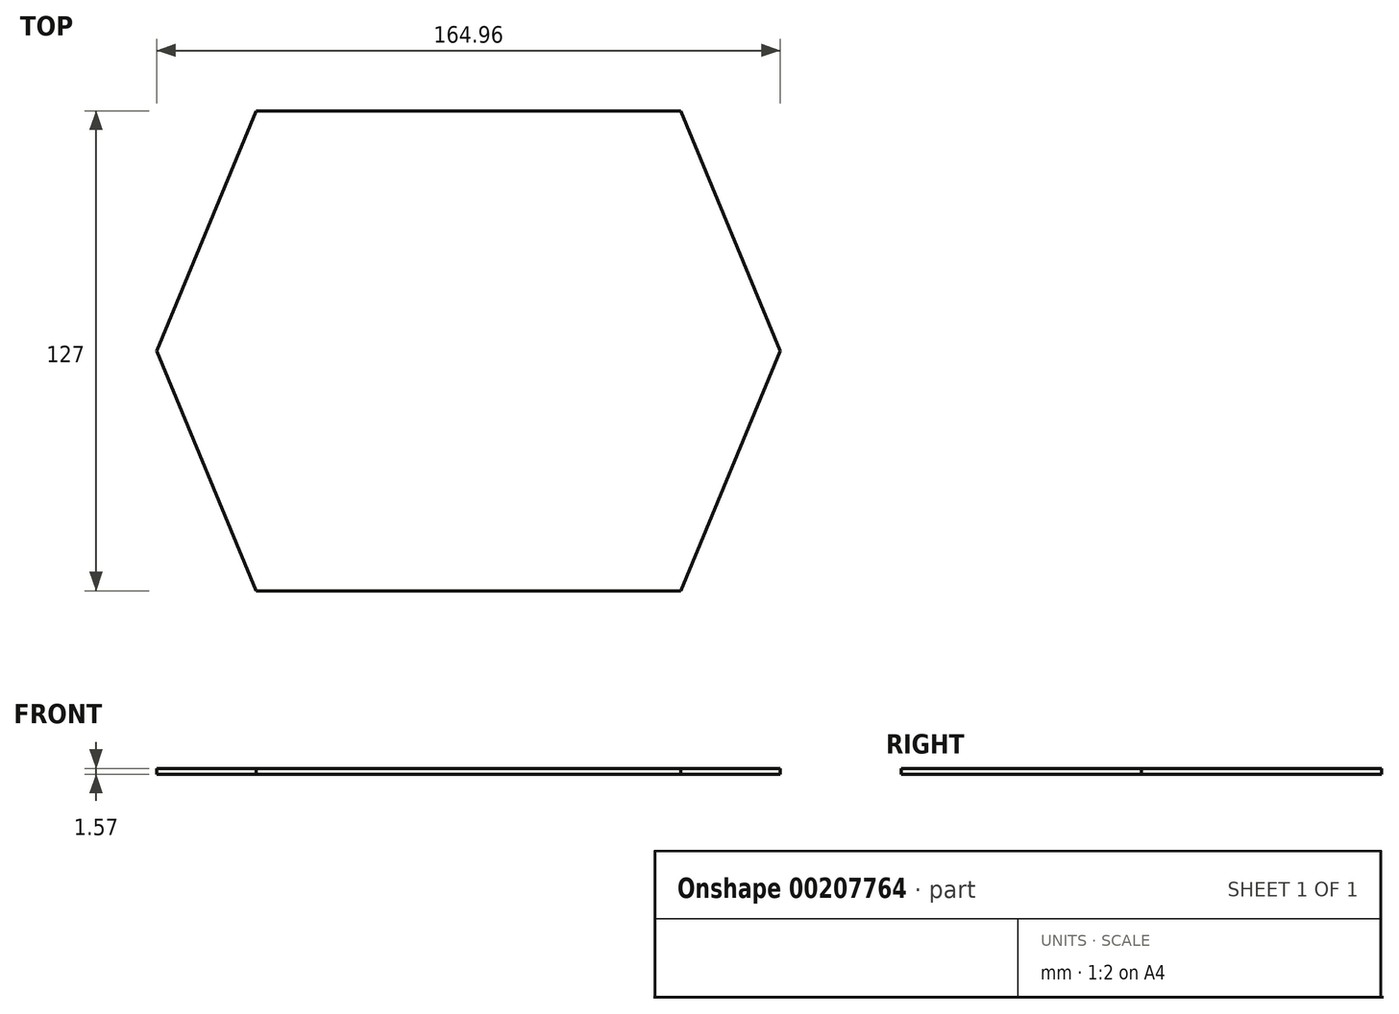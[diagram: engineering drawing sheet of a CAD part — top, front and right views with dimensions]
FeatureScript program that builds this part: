
annotation { "Feature Type Name" : "Feature", "Feature Type Description" : "" }
export const myFeature = defineFeature(function(context is Context, id is Id, definition is map)
    precondition{}
    {
        {
            var Q0;
            Q0=qCreatedBy(makeId("Top.planeOp"),FACE);
            var sketch = newSketch(context, id + "F0", { "sketchPlane" : qUnion([Q0])});
            skLineSegment(sketch, "E0", {"start": v(-56.18, 63.5) * mm, "end": v(56.18, 63.5) * mm});
            skLineSegment(sketch, "E1", {"start": v(-56.18, -63.5) * mm, "end": v(56.18, -63.5) * mm});
            skLineSegment(sketch, "E2", {"start": v(56.18, -63.5) * mm, "end": v(82.48, 0) * mm});
            skLineSegment(sketch, "E3", {"start": v(82.48, 0) * mm, "end": v(56.18, 63.5) * mm});
            skLineSegment(sketch, "E4", {"start": v(-56.18, -63.5) * mm, "end": v(-82.48, 0) * mm});
            skLineSegment(sketch, "E5", {"start": v(-82.48, 0) * mm, "end": v(-56.18, 63.5) * mm});
            skLineSegment(sketch, "E6", {"start": v(-82.48, 0) * mm, "end": v(82.48, 0) * mm, "construction": true});
            skSolve(sketch);
        }
        {
            var Q0;
            Q0 = qSketchRegion(id + "F0", true);
            extrude(context, id + "F1", {"entities" : qUnion([Q0]), "depth" : 1.57 * mm});
        }
    });
